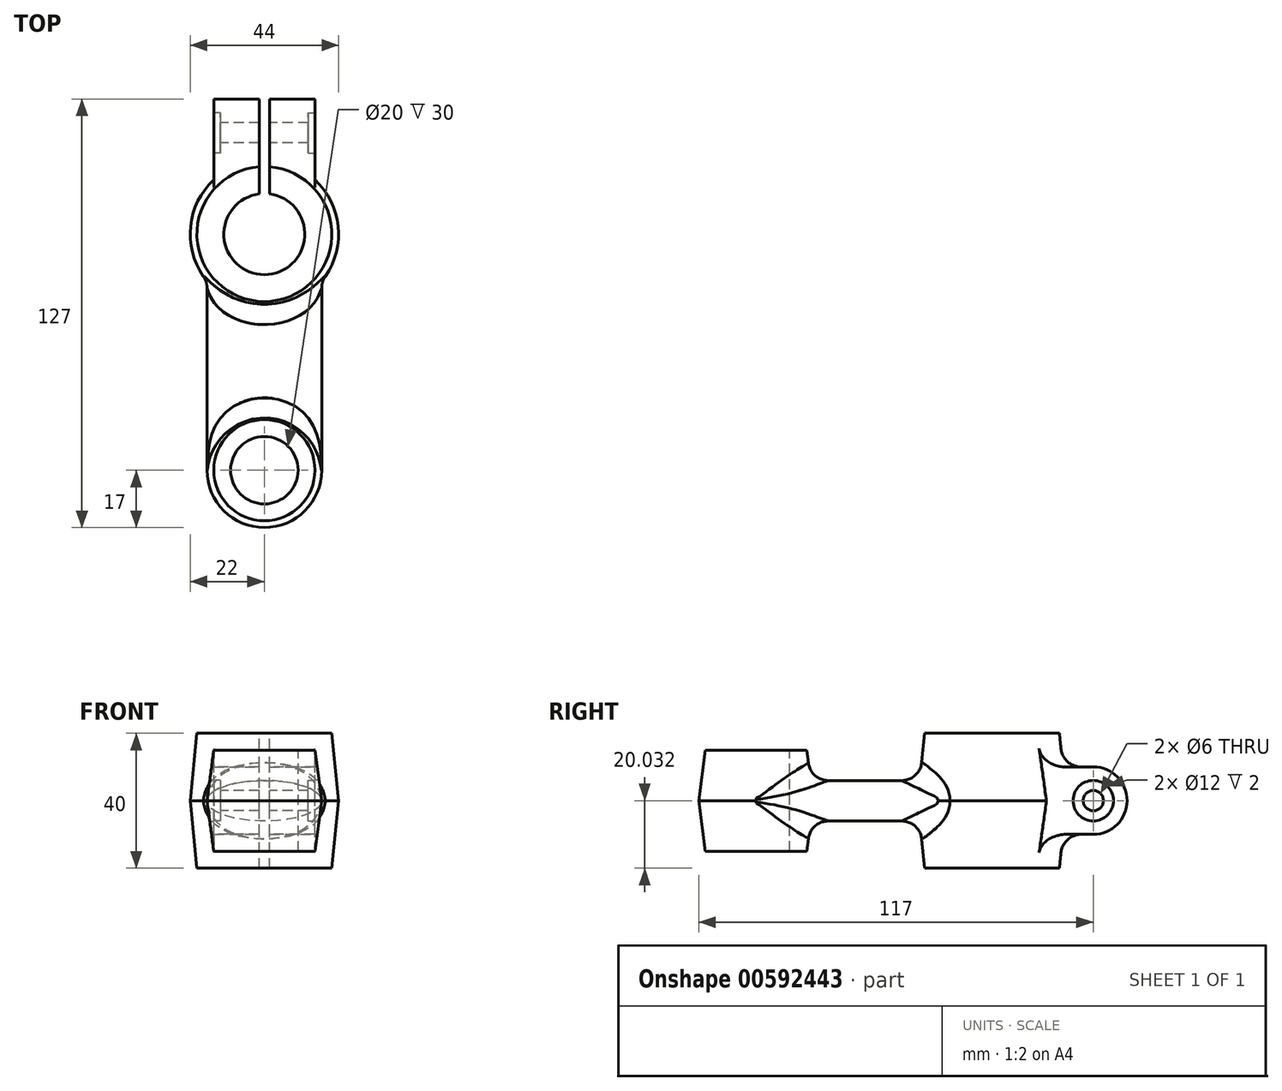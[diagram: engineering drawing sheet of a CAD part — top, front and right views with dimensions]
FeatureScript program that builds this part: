
annotation { "Feature Type Name" : "Feature", "Feature Type Description" : "" }
export const myFeature = defineFeature(function(context is Context, id is Id, definition is map)
    precondition{}
    {
        {
            var Q0;
            Q0=qCreatedBy(makeId("Front.planeOp"),FACE);
            var sketch = newSketch(context, id + "F0", { "sketchPlane" : qUnion([Q0])});
            skEllipse(sketch, "E0", {"center": v(0, 0) * mm, "majorRadius": 17 * mm, "minorRadius": 6 * mm, "majorAxis": v(1, 0)});
            skSolve(sketch);
        }
        {
            var Q0;
            Q0 = qSketchRegion(id + "F0", true);
            extrude(context, id + "F1", {"entities" : qUnion([Q0]), "depth" : 70 * mm, "offsetDistance" : 25 * mm});
        }
        {
            var Q0;
            Q0=qCreatedBy(makeId("Right.planeOp"),FACE);
            var sketch = newSketch(context, id + "F2", { "sketchPlane" : qUnion([Q0])});
            skLineSegment(sketch, "E1", {"start": v(20, 20) * mm, "end": v(0, 20) * mm});
            skLineSegment(sketch, "E2", {"start": v(20, 20) * mm, "end": v(22, 0) * mm});
            skLineSegment(sketch, "E3", {"start": v(22, 0) * mm, "end": v(20, -20) * mm});
            skLineSegment(sketch, "E4", {"start": v(20, -20) * mm, "end": v(0, -20) * mm});
            skLineSegment(sketch, "E5", {"start": v(0, -20) * mm, "end": v(0, 20) * mm});
            skSolve(sketch);
        }
        {
            var Q0;
            Q0 = qSketchRegion(id + "F2", true);
            var Q1;
            Q1=sQuery(id+"F2.wireOp",EDGE,"E5");
            revolve(context, id + "F3", {"operationType" : NewBodyOperationType.ADD, "entities" : qUnion([Q0]), "axis" : qUnion([Q1]), "revolveType" : RevolveType.FULL});
        }
        {
            var Q0;
            Q0=qCreatedBy(makeId("Right.planeOp"),FACE);
            var sketch = newSketch(context, id + "F4", { "sketchPlane" : qUnion([Q0])});
            skLineSegment(sketch, "E6", {"start": v(-70, 0) * mm, "end": v(-70, 15) * mm});
            skLineSegment(sketch, "E7", {"start": v(-70, 15) * mm, "end": v(-85, 15) * mm});
            skLineSegment(sketch, "E8", {"start": v(-85, 15) * mm, "end": v(-87, 0) * mm});
            skLineSegment(sketch, "E9", {"start": v(-87, 0) * mm, "end": v(-85, -15) * mm});
            skLineSegment(sketch, "E10", {"start": v(-85, -15) * mm, "end": v(-70, -15) * mm});
            skLineSegment(sketch, "E11", {"start": v(-70, -15) * mm, "end": v(-70, 0) * mm});
            skSolve(sketch);
        }
        {
            var Q0;
            Q0 = qSketchRegion(id + "F4", true);
            var Q1;
            Q1=sQuery(id+"F4.wireOp",EDGE,"E6");
            revolve(context, id + "F5", {"operationType" : NewBodyOperationType.ADD, "entities" : qUnion([Q0]), "axis" : qUnion([Q1]), "revolveType" : RevolveType.FULL});
        }
        {
            var Q0;
            Q0=makeQuery(id+"F3.boolean.opBoolean","INTERSECT",EDGE,{"derivedFrom":[makeQuery(id+"F1.opExtrude","SWEPT_FACE",FACE,{"disambiguationData":[OSD([sQuery(id+"F0.wireOp",EDGE,"E0")])]}),makeQuery(id+"F3.opRevolve","SWEPT_FACE",FACE,{"disambiguationData":[OSD([sQuery(id+"F2.wireOp",EDGE,"E3")])]})]});
            var Q1;
            Q1=makeQuery(id+"F3.boolean.opBoolean","INTERSECT",EDGE,{"derivedFrom":[makeQuery(id+"F1.opExtrude","SWEPT_FACE",FACE,{"disambiguationData":[OSD([sQuery(id+"F0.wireOp",EDGE,"E0")])]}),makeQuery(id+"F3.opRevolve","SWEPT_FACE",FACE,{"disambiguationData":[OSD([sQuery(id+"F2.wireOp",EDGE,"E2")])]})]});
            var Q2;
            Q2=makeQuery(id+"F5.boolean.opBoolean","INTERSECT",EDGE,{"derivedFrom":[makeQuery(id+"F1.opExtrude","SWEPT_FACE",FACE,{"disambiguationData":[OSD([sQuery(id+"F0.wireOp",EDGE,"E0")])]}),makeQuery(id+"F5.opRevolve","SWEPT_FACE",FACE,{"disambiguationData":[OSD([sQuery(id+"F4.wireOp",EDGE,"E9")])]})]});
            var Q3;
            Q3=makeQuery(id+"F5.boolean.opBoolean","INTERSECT",EDGE,{"derivedFrom":[makeQuery(id+"F1.opExtrude","SWEPT_FACE",FACE,{"disambiguationData":[OSD([sQuery(id+"F0.wireOp",EDGE,"E0")])]}),makeQuery(id+"F5.opRevolve","SWEPT_FACE",FACE,{"disambiguationData":[OSD([sQuery(id+"F4.wireOp",EDGE,"E8")])]})]});
            fillet(context, id + "F6", {"entities" : qUnion([Q0, Q1, Q2, Q3]), "radius" : 6 * mm, "tangentPropagation" : true, "allowEdgeOverflow" : false});
        }
        {
            var Q0;
            Q0=makeQuery(id+"F3.opRevolve","SWEPT_FACE",FACE,{"disambiguationData":[OSD([sQuery(id+"F2.wireOp",EDGE,"E1")])]});
            var sketch = newSketch(context, id + "F7", { "sketchPlane" : qUnion([Q0])});
            skCircle(sketch, "E12", {"center": v(0, 0) * mm, "radius": 12 * mm});
            skSolve(sketch);
        }
        {
            var Q0;
            Q0=makeQuery(id+"F7.imprint","IMPRINT",FACE,{"disambiguationData":[TD([[makeQuery(id+"F7.imprint","IMPRINT",EDGE,{"derivedFrom":sQuery(id+"F7.wireOp",EDGE,"E12")}),1.0]])]});
            extrude(context, id + "F8", {"entities" : qUnion([Q0]), "operationType" : NewBodyOperationType.REMOVE, "endBound" : BoundingType.THROUGH_ALL, "oppositeDirection" : true, "depth" : 25 * mm, "offsetDistance" : 25 * mm});
        }
        {
            var Q0;
            Q0=makeQuery(id+"F5.opRevolve","SWEPT_FACE",FACE,{"disambiguationData":[OSD([sQuery(id+"F4.wireOp",EDGE,"E7")])]});
            var sketch = newSketch(context, id + "F9", { "sketchPlane" : qUnion([Q0])});
            skCircle(sketch, "E13", {"center": v(0, -70) * mm, "radius": 10 * mm});
            skSolve(sketch);
        }
        {
            var Q0;
            Q0=makeQuery(id+"F9.imprint","IMPRINT",FACE,{"disambiguationData":[TD([[makeQuery(id+"F9.imprint","IMPRINT",EDGE,{"derivedFrom":sQuery(id+"F9.wireOp",EDGE,"E13")}),1.0]])]});
            extrude(context, id + "F10", {"entities" : qUnion([Q0]), "operationType" : NewBodyOperationType.REMOVE, "endBound" : BoundingType.THROUGH_ALL, "oppositeDirection" : true, "depth" : 25 * mm, "offsetDistance" : 25 * mm});
        }
        {
            var Q0;
            Q0=qCreatedBy(makeId("Right.planeOp"),FACE);
            var sketch = newSketch(context, id + "F11", { "sketchPlane" : qUnion([Q0])});
            skLineSegment(sketch, "E14.bottom", {"start": v(30, 10.03) * mm, "end": v(0, 10.03) * mm});
            skLineSegment(sketch, "E14.top", {"start": v(30, -9.97) * mm, "end": v(0, -9.97) * mm});
            skLineSegment(sketch, "E14.left", {"start": v(30, 10.03) * mm, "end": v(30, -9.97) * mm});
            skArc(sketch, "E15", {"start": v(30, -9.97) * mm, "mid": v(40, 0.03) * mm, "end": v(30, 10.03) * mm});
            skLineSegment(sketch, "E16", {"start": v(0, 10.03) * mm, "end": v(0, -9.97) * mm});
            skSolve(sketch);
        }
        {
            var Q0;
            Q0 = qSketchRegion(id + "F11", true);
            extrude(context, id + "F12", {"entities" : qUnion([Q0]), "operationType" : NewBodyOperationType.ADD, "endBound" : BoundingType.SYMMETRIC, "depth" : 30 * mm, "offsetDistance" : 25 * mm});
        }
        {
            var Q0;
            Q0=makeQuery(id+"F12.opExtrude","CAP_FACE",FACE,{"disambiguationData":[OSD([sQuery(id+"F11.wireOp",EDGE,"E14.bottom"),sQuery(id+"F11.wireOp",EDGE,"E14.top"),sQuery(id+"F11.wireOp",EDGE,"E15"),sQuery(id+"F11.wireOp",EDGE,"E16")])],"isStart":true});
            var sketch = newSketch(context, id + "F13", { "sketchPlane" : qUnion([Q0])});
            skCircle(sketch, "E17", {"center": v(-30, 0.03) * mm, "radius": 6 * mm});
            skSolve(sketch);
        }
        {
            var Q0;
            Q0 = qSketchRegion(id + "F13", true);
            extrude(context, id + "F14", {"entities" : qUnion([Q0]), "operationType" : NewBodyOperationType.REMOVE, "oppositeDirection" : true, "depth" : 2 * mm, "offsetDistance" : 25 * mm});
        }
        {
            var Q0;
            Q0=makeQuery(id+"F12.opExtrude","CAP_FACE",FACE,{"disambiguationData":[OSD([sQuery(id+"F11.wireOp",EDGE,"E14.bottom"),sQuery(id+"F11.wireOp",EDGE,"E14.top"),sQuery(id+"F11.wireOp",EDGE,"E15"),sQuery(id+"F11.wireOp",EDGE,"E16")])],"isStart":false});
            var sketch = newSketch(context, id + "F15", { "sketchPlane" : qUnion([Q0])});
            skCircle(sketch, "E18", {"center": v(30, 0.03) * mm, "radius": 6 * mm});
            skSolve(sketch);
        }
        {
            var Q0;
            Q0 = qSketchRegion(id + "F15", true);
            extrude(context, id + "F16", {"entities" : qUnion([Q0]), "operationType" : NewBodyOperationType.REMOVE, "oppositeDirection" : true, "depth" : 2 * mm, "offsetDistance" : 25 * mm});
        }
        {
            var Q0;
            Q0=makeQuery(id+"F14.boolean.opBoolean","COPY",FACE,{"derivedFrom":makeQuery(id+"F14.opExtrude","CAP_FACE",FACE,{"disambiguationData":[OSD([sQuery(id+"F13.wireOp",EDGE,"E17")])],"isStart":false})});
            var sketch = newSketch(context, id + "F17", { "sketchPlane" : qUnion([Q0])});
            skCircle(sketch, "E19", {"center": v(-30, 0.03) * mm, "radius": 3 * mm});
            skSolve(sketch);
        }
        {
            var Q0;
            Q0 = qSketchRegion(id + "F17", true);
            extrude(context, id + "F18", {"entities" : qUnion([Q0]), "operationType" : NewBodyOperationType.REMOVE, "endBound" : BoundingType.THROUGH_ALL, "oppositeDirection" : true, "depth" : 25 * mm, "offsetDistance" : 25 * mm});
        }
        {
            var Q0;
            Q0=makeQuery(id+"F12.boolean.opBoolean","INTERSECT",EDGE,{"derivedFrom":[makeQuery(id+"F3.opRevolve","SWEPT_FACE",FACE,{"disambiguationData":[OSD([sQuery(id+"F2.wireOp",EDGE,"E2")])]}),makeQuery(id+"F12.opExtrude","SWEPT_FACE",FACE,{"disambiguationData":[OSD([sQuery(id+"F11.wireOp",EDGE,"E14.bottom")])]})]});
            var Q1;
            Q1=makeQuery(id+"F12.boolean.opBoolean","INTERSECT",EDGE,{"derivedFrom":[makeQuery(id+"F3.opRevolve","SWEPT_FACE",FACE,{"disambiguationData":[OSD([sQuery(id+"F2.wireOp",EDGE,"E3")])]}),makeQuery(id+"F12.opExtrude","SWEPT_FACE",FACE,{"disambiguationData":[OSD([sQuery(id+"F11.wireOp",EDGE,"E14.top")])]})]});
            fillet(context, id + "F19", {"entities" : qUnion([Q0, Q1]), "radius" : 6 * mm, "tangentPropagation" : true, "allowEdgeOverflow" : false});
        }
        {
            var Q0;
            Q0=makeQuery(id+"F12.boolean.opBoolean","SPLIT",FACE,{"disambiguationData":[TD([makeQuery(id+"F8.boolean.opBoolean","COPY",FACE,{"derivedFrom":makeQuery(id+"F8.opExtrude","SWEPT_FACE",FACE,{"disambiguationData":[OSD([sQuery(id+"F7.wireOp",EDGE,"E12")])]})})])],"derivedFrom":makeQuery(id+"F12.opExtrude","SWEPT_FACE",FACE,{"disambiguationData":[OSD([sQuery(id+"F11.wireOp",EDGE,"E14.bottom")])]})});
            extrude(context, id + "F20", {"entities" : qUnion([Q0]), "operationType" : NewBodyOperationType.REMOVE, "endBound" : BoundingType.THROUGH_ALL, "oppositeDirection" : true, "depth" : 25 * mm, "offsetDistance" : 25 * mm});
        }
        {
            var Q0;
            Q0=makeQuery(id+"F3.opRevolve","SWEPT_FACE",FACE,{"disambiguationData":[OSD([sQuery(id+"F2.wireOp",EDGE,"E1")])]});
            var sketch = newSketch(context, id + "F21", { "sketchPlane" : qUnion([Q0])});
            skLineSegment(sketch, "E20.0", {"start": v(-1.5, 0) * mm, "end": v(-1.5, 45.74) * mm});
            skLineSegment(sketch, "E21.0", {"start": v(1.5, 0) * mm, "end": v(1.5, 45.74) * mm});
            skLineSegment(sketch, "E22", {"start": v(-1.5, 45.74) * mm, "end": v(1.5, 45.74) * mm});
            skLineSegment(sketch, "E23", {"start": v(1.5, 0) * mm, "end": v(-1.5, 0) * mm});
            skPoint(sketch, "E24.start.orphan", {"position": v(0, 0) * mm});
            skSolve(sketch);
        }
        {
            var Q0;
            Q0 = qSketchRegion(id + "F21", true);
            extrude(context, id + "F22", {"entities" : qUnion([Q0]), "operationType" : NewBodyOperationType.REMOVE, "endBound" : BoundingType.THROUGH_ALL, "oppositeDirection" : true, "depth" : 25 * mm, "offsetDistance" : 25 * mm});
        }
    });
